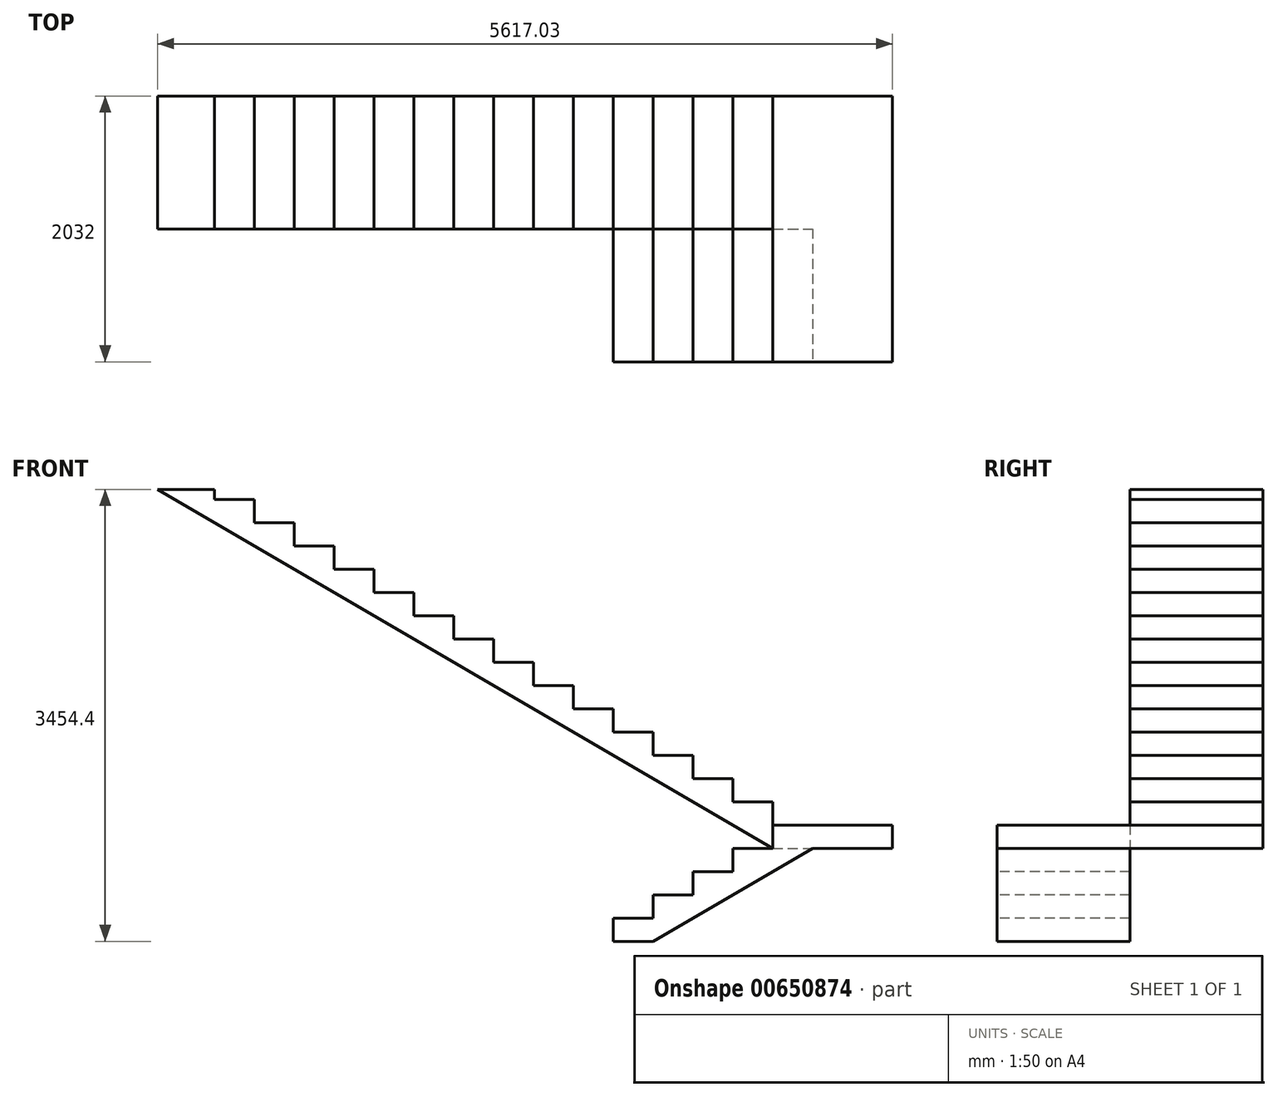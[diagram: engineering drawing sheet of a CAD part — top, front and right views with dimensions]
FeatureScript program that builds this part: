
annotation { "Feature Type Name" : "Feature", "Feature Type Description" : "" }
export const myFeature = defineFeature(function(context is Context, id is Id, definition is map)
    precondition{}
    {
        {
            var Q0;
            Q0=qCreatedBy(makeId("Top.planeOp"),FACE);
            var sketch = newSketch(context, id + "F0", { "sketchPlane" : qUnion([Q0])});
            skLineSegment(sketch, "E0.bottom", {"start": v(0, 0) * mm, "end": v(-9144, 0) * mm});
            skLineSegment(sketch, "E0.top", {"start": v(0, -2032) * mm, "end": v(-9144, -2032) * mm});
            skLineSegment(sketch, "E0.left", {"start": v(0, 0) * mm, "end": v(0, -2032) * mm});
            skLineSegment(sketch, "E0.right", {"start": v(-9144, 0) * mm, "end": v(-9144, -2032) * mm});
            skSolve(sketch);
        }
        {
            var Q0;
            Q0=makeQuery(id+"F0.imprint","IMPRINT",FACE,{"disambiguationData":[TD([[makeQuery(id+"F0.imprint","IMPRINT",EDGE,{"derivedFrom":sQuery(id+"F0.wireOp",EDGE,"E0.bottom")}),1.0]])]});
            extrude(context, id + "F1", {"entities" : qUnion([Q0]), "depth" : 3454.4 * mm, "offsetDistance" : 25.4 * mm});
        }
        {
            var Q0;
            Q0=makeQuery(id+"F1.opExtrude","SWEPT_FACE",FACE,{"disambiguationData":[OSD([sQuery(id+"F0.wireOp",EDGE,"E0.top")])]});
            var sketch = newSketch(context, id + "F2", { "sketchPlane" : qUnion([Q0])});
            skLineSegment(sketch, "E1", {"start": v(-2133.6, 0) * mm, "end": v(-2133.6, 177.8) * mm});
            skLineSegment(sketch, "E2", {"start": v(-2133.6, 177.8) * mm, "end": v(-1828.8, 177.8) * mm});
            skLineSegment(sketch, "E3", {"start": v(-1828.8, 177.8) * mm, "end": v(-2133.6, 0) * mm, "construction": true});
            skLineSegment(sketch, "E4", {"start": v(-1828.8, 177.8) * mm, "end": v(-1828.8, 355.6) * mm});
            skLineSegment(sketch, "E5", {"start": v(-1828.8, 355.6) * mm, "end": v(-1524, 355.6) * mm});
            skLineSegment(sketch, "E6", {"start": v(-1524, 355.6) * mm, "end": v(-1524, 533.4) * mm});
            skLineSegment(sketch, "E7", {"start": v(-1524, 533.4) * mm, "end": v(-1219.2, 533.4) * mm});
            skLineSegment(sketch, "E8", {"start": v(-1219.2, 533.4) * mm, "end": v(-1219.2, 711.2) * mm});
            skLineSegment(sketch, "E9", {"start": v(-1219.2, 711.2) * mm, "end": v(-914.4, 711.2) * mm});
            skLineSegment(sketch, "E10", {"start": v(-914.4, 889) * mm, "end": v(0, 889) * mm});
            skLineSegment(sketch, "E11", {"start": v(0, 889) * mm, "end": v(0, 3454.4) * mm});
            skLineSegment(sketch, "E12", {"start": v(0, 3454.4) * mm, "end": v(-9144, 3454.4) * mm});
            skLineSegment(sketch, "E13", {"start": v(-9144, 3454.4) * mm, "end": v(-9144, 0) * mm});
            skLineSegment(sketch, "E14", {"start": v(-9144, 0) * mm, "end": v(-2133.6, 0) * mm});
            skLineSegment(sketch, "E15", {"start": v(-914.4, 889) * mm, "end": v(-914.4, 711.2) * mm});
            skLineSegment(sketch, "E16", {"start": v(-1828.8, 0) * mm, "end": v(-609.6, 711.2) * mm});
            skLineSegment(sketch, "E17", {"start": v(-609.6, 711.2) * mm, "end": v(0, 711.2) * mm});
            skLineSegment(sketch, "E18", {"start": v(-2340.5, -5.39) * mm, "end": v(-2341.27, 0) * mm});
            skSolve(sketch);
        }
        {
            var Q0;
            Q0=makeQuery(id+"F2.imprint","IMPRINT",FACE,{"disambiguationData":[TD([[makeQuery(id+"F2.imprint","IMPRINT",EDGE,{"derivedFrom":sQuery(id+"F2.wireOp",EDGE,"E1")}),1.0]])]});
            var Q1;
            {var subQ0=sQuery(id+"F2.wireOp",EDGE,"E16");Q1=makeQuery(id+"F2.imprint","IMPRINT",FACE,{"disambiguationData":[TD([[makeQuery(id+"F2.imprint","IMPRINT",EDGE,{"derivedFrom":subQ0}),-1.0]])]});}
            extrude(context, id + "F3", {"entities" : qUnion([Q0, Q1]), "operationType" : NewBodyOperationType.REMOVE, "oppositeDirection" : true, "depth" : 1016 * mm, "offsetDistance" : 25.4 * mm});
        }
        {
            var Q0;
            Q0=makeQuery(id+"F3.boolean.opBoolean","COPY",FACE,{"derivedFrom":makeQuery(id+"F3.opExtrude","CAP_FACE",FACE,{"disambiguationData":[OSD([sQuery(id+"F2.wireOp",EDGE,"E1"),sQuery(id+"F2.wireOp",EDGE,"E2"),sQuery(id+"F2.wireOp",EDGE,"E4"),sQuery(id+"F2.wireOp",EDGE,"E5"),sQuery(id+"F2.wireOp",EDGE,"E6"),sQuery(id+"F2.wireOp",EDGE,"E7"),sQuery(id+"F2.wireOp",EDGE,"E8"),sQuery(id+"F2.wireOp",EDGE,"E9"),sQuery(id+"F2.wireOp",EDGE,"a5Cy1vTD-OkmN-O4y6-2xoB-Rp8nYggBoZmQ"),sQuery(id+"F2.wireOp",EDGE,"GUVeX8nQ-cmAj-bjHG-ShmB-PFHY6lqEPjUW"),sQuery(id+"F2.wireOp",EDGE,"1bp7qSfN-vpIR-g9EB-JvXt-JwCoal104RiD"),sQuery(id+"F2.wireOp",EDGE,"csJfhYp6-8XFc-QxRr-4XWy-1mM8NWqT7x9U"),sQuery(id+"F2.wireOp",EDGE,"Q1kJw1lr-qJOf-uzbH-V3sw-y8dtpFdwQhgd"),sQuery(id+"F2.wireOp",EDGE,"Gtidlj7p-xUDf-JRcw-XCZD-ExYsw8wxzXof"),sQuery(id+"F2.wireOp",EDGE,"vgk84In2-5dPP-45W6-IbeS-nH1OyMuFnZ1p"),sQuery(id+"F2.wireOp",EDGE,"E10"),sQuery(id+"F2.wireOp",EDGE,"E11"),sQuery(id+"F2.wireOp",EDGE,"E12"),sQuery(id+"F2.wireOp",EDGE,"E13"),sQuery(id+"F2.wireOp",EDGE,"E14")])],"isStart":false})});
            var sketch = newSketch(context, id + "F4", { "sketchPlane" : qUnion([Q0])});
            skLineSegment(sketch, "E19", {"start": v(-914.4, 889) * mm, "end": v(-914.4, 1066.8) * mm});
            skLineSegment(sketch, "E20", {"start": v(-914.4, 1066.8) * mm, "end": v(-1219.2, 1066.8) * mm});
            skLineSegment(sketch, "E21", {"start": v(-1219.2, 1066.8) * mm, "end": v(-1219.2, 1244.6) * mm});
            skLineSegment(sketch, "E22", {"start": v(-1219.2, 1244.6) * mm, "end": v(-1524, 1244.6) * mm});
            skLineSegment(sketch, "E23", {"start": v(-1524, 1244.6) * mm, "end": v(-1524, 1422.4) * mm});
            skLineSegment(sketch, "E24", {"start": v(-1524, 1422.4) * mm, "end": v(-1828.8, 1422.4) * mm});
            skLineSegment(sketch, "E25", {"start": v(-1828.8, 1422.4) * mm, "end": v(-1828.8, 1600.2) * mm});
            skLineSegment(sketch, "E26", {"start": v(-1828.8, 1600.2) * mm, "end": v(-2133.6, 1600.2) * mm});
            skLineSegment(sketch, "E27", {"start": v(-2133.6, 1600.2) * mm, "end": v(-2133.6, 1778) * mm});
            skLineSegment(sketch, "E28", {"start": v(-2133.6, 1778) * mm, "end": v(-2438.4, 1778) * mm});
            skLineSegment(sketch, "E29", {"start": v(-2438.4, 1778) * mm, "end": v(-2438.4, 1955.8) * mm});
            skLineSegment(sketch, "E30", {"start": v(-2438.4, 1955.8) * mm, "end": v(-2743.2, 1955.8) * mm});
            skLineSegment(sketch, "E31", {"start": v(-2743.2, 1955.8) * mm, "end": v(-2743.2, 2133.6) * mm});
            skLineSegment(sketch, "E32", {"start": v(-2743.2, 2133.6) * mm, "end": v(-3048, 2133.6) * mm});
            skLineSegment(sketch, "E33", {"start": v(-3048, 2133.6) * mm, "end": v(-3048, 2311.4) * mm});
            skLineSegment(sketch, "E34", {"start": v(-3048, 2311.4) * mm, "end": v(-3352.8, 2311.4) * mm});
            skLineSegment(sketch, "E35", {"start": v(-3352.8, 2311.4) * mm, "end": v(-3352.8, 2489.2) * mm});
            skLineSegment(sketch, "E36", {"start": v(0, 3454.4) * mm, "end": v(0, 889) * mm});
            skLineSegment(sketch, "E37", {"start": v(0, 889) * mm, "end": v(-914.4, 889) * mm});
            skLineSegment(sketch, "E38", {"start": v(-1524, 1244.6) * mm, "end": v(-1219.2, 1066.8) * mm, "construction": true});
            skLineSegment(sketch, "E39", {"start": v(-914.4, 711.2) * mm, "end": v(0, 711.2) * mm});
            skLineSegment(sketch, "E40", {"start": v(0, 711.2) * mm, "end": v(0, 0) * mm});
            skLineSegment(sketch, "E41", {"start": v(0, 0) * mm, "end": v(-9144, 0) * mm});
            skLineSegment(sketch, "E42", {"start": v(-3352.8, 2489.2) * mm, "end": v(-3657.6, 2489.2) * mm});
            skLineSegment(sketch, "E43", {"start": v(-3657.6, 2489.2) * mm, "end": v(-3657.6, 2667) * mm});
            skLineSegment(sketch, "E44", {"start": v(-3657.6, 2667) * mm, "end": v(-3962.4, 2667) * mm});
            skLineSegment(sketch, "E45", {"start": v(-3962.4, 2667) * mm, "end": v(-3962.4, 2844.8) * mm});
            skLineSegment(sketch, "E46", {"start": v(-3962.4, 2844.8) * mm, "end": v(-4267.2, 2844.8) * mm});
            skLineSegment(sketch, "E47", {"start": v(-4267.2, 2844.8) * mm, "end": v(-4267.2, 3022.6) * mm});
            skLineSegment(sketch, "E48", {"start": v(-4267.2, 3022.6) * mm, "end": v(-4572, 3022.6) * mm});
            skLineSegment(sketch, "E49", {"start": v(-914.4, 711.2) * mm, "end": v(-5617.03, 3454.4) * mm});
            skLineSegment(sketch, "E50", {"start": v(-9144, 3454.4) * mm, "end": v(-9144, 0) * mm});
            skLineSegment(sketch, "E51", {"start": v(-4572, 3022.6) * mm, "end": v(-4572, 3200.4) * mm});
            skLineSegment(sketch, "E52", {"start": v(-4572, 3200.4) * mm, "end": v(-4876.8, 3200.4) * mm});
            skLineSegment(sketch, "E53", {"start": v(-4876.8, 3200.4) * mm, "end": v(-4876.8, 3378.2) * mm});
            skLineSegment(sketch, "E54", {"start": v(-4876.8, 3378.2) * mm, "end": v(-5181.6, 3378.2) * mm});
            skLineSegment(sketch, "E55", {"start": v(-5181.6, 3378.2) * mm, "end": v(-5181.6, 3454.4) * mm});
            skLineSegment(sketch, "E56", {"start": v(-5181.6, 3454.4) * mm, "end": v(0, 3454.4) * mm});
            skLineSegment(sketch, "E57", {"start": v(-5617.03, 3454.4) * mm, "end": v(-9144, 3454.4) * mm});
            skSolve(sketch);
        }
        {
            var Q0;
            Q0=makeQuery(id+"F4.imprint","IMPRINT",FACE,{"disambiguationData":[TD([[makeQuery(id+"F4.imprint","IMPRINT",EDGE,{"derivedFrom":sQuery(id+"F4.wireOp",EDGE,"rlm9xth9-klbt-0tqx-mV7Z-GZkHHSqsjoMw")}),-1.0]])]});
            var Q1;
            Q1=makeQuery(id+"F4.imprint","IMPRINT",FACE,{"disambiguationData":[TD([[makeQuery(id+"F4.imprint","IMPRINT",EDGE,{"derivedFrom":sQuery(id+"F4.wireOp",EDGE,"E49")}),1.0]])]});
            var Q2;
            Q2=makeQuery(id+"F4.imprint","IMPRINT",FACE,{"disambiguationData":[TD([[makeQuery(id+"F4.imprint","IMPRINT",EDGE,{"derivedFrom":sQuery(id+"F4.wireOp",EDGE,"E19")}),-1.0]])]});
            var Q3;
            Q3=makeQuery(id+"F4.imprint","IMPRINT",FACE,{"disambiguationData":[TD([[makeQuery(id+"F4.imprint","IMPRINT",EDGE,{"derivedFrom":sQuery(id+"F4.wireOp",EDGE,"E39")}),-1.0]])]});
            extrude(context, id + "F5", {"entities" : qUnion([Q0, Q1, Q2, Q3]), "operationType" : NewBodyOperationType.REMOVE, "endBound" : BoundingType.UP_TO_NEXT, "oppositeDirection" : true, "depth" : 25.4 * mm, "offsetDistance" : 25.4 * mm});
        }
    });
